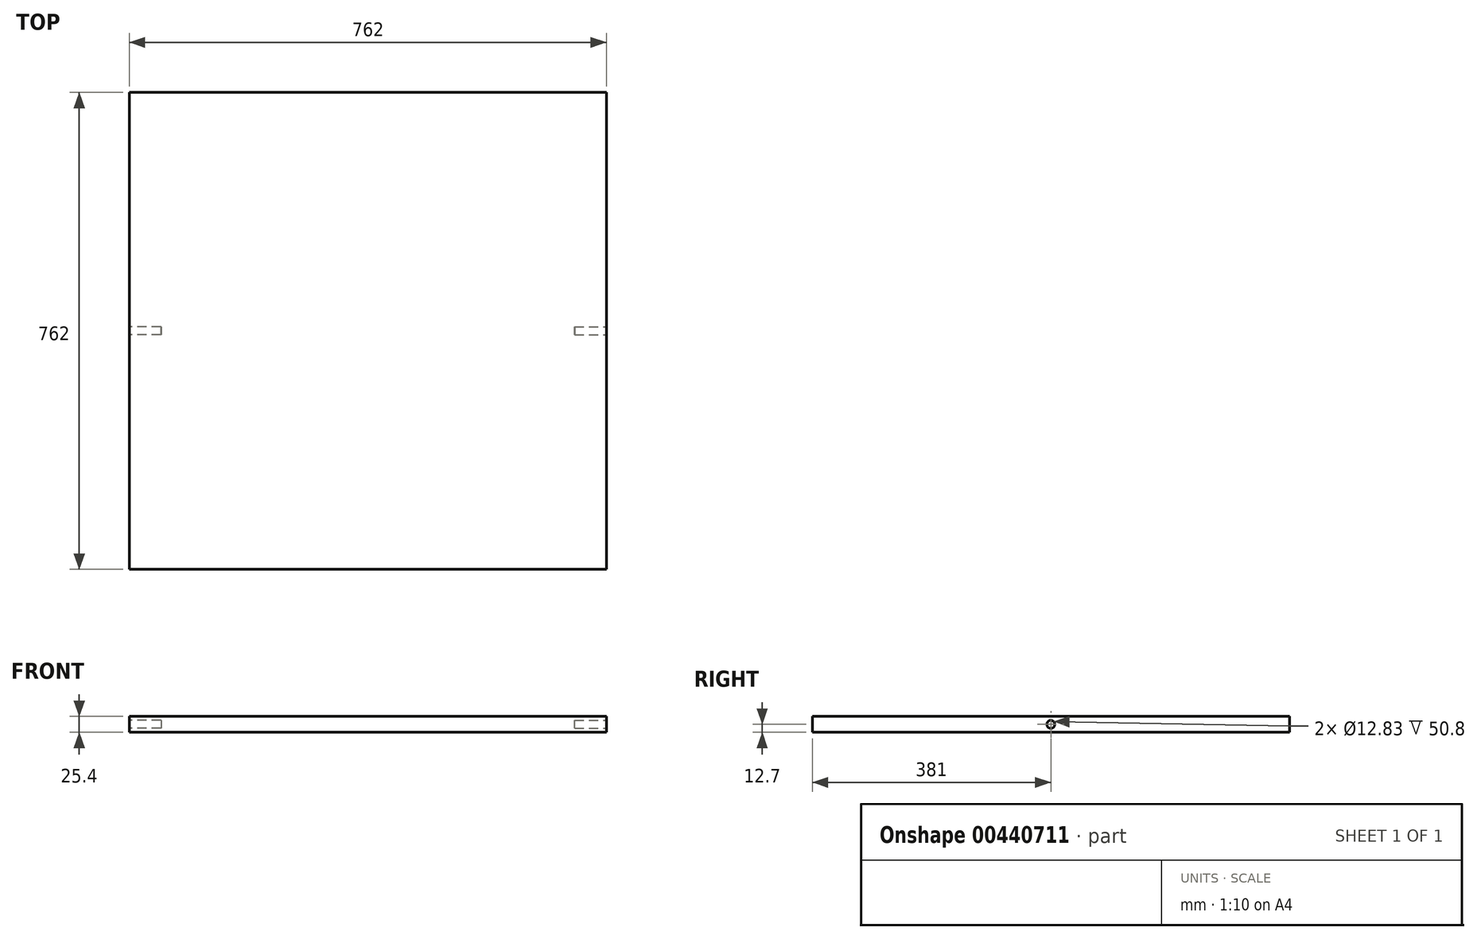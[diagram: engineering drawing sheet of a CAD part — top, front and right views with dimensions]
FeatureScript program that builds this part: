
annotation { "Feature Type Name" : "Feature", "Feature Type Description" : "" }
export const myFeature = defineFeature(function(context is Context, id is Id, definition is map)
    precondition{}
    {
        {
            var Q0;
            Q0=qCreatedBy(makeId("Top.planeOp"),FACE);
            var sketch = newSketch(context, id + "F0", { "sketchPlane" : qUnion([Q0])});
            skLineSegment(sketch, "E0.bottom", {"start": v(-381, 381) * mm, "end": v(381, 381) * mm});
            skLineSegment(sketch, "E0.top", {"start": v(-381, -381) * mm, "end": v(381, -381) * mm});
            skLineSegment(sketch, "E0.left", {"start": v(-381, 381) * mm, "end": v(-381, -381) * mm});
            skLineSegment(sketch, "E0.right", {"start": v(381, 381) * mm, "end": v(381, -381) * mm});
            skPoint(sketch, "E0.middle", {"position": v(0, 0) * mm});
            skSolve(sketch);
        }
        {
            var Q0;
            Q0 = qSketchRegion(id + "F0", true);
            extrude(context, id + "F1", {"entities" : qUnion([Q0]), "depth" : 25.4 * mm});
        }
        {
            var Q0;
            Q0=makeQuery(id+"F1.opExtrude","SWEPT_FACE",FACE,{"disambiguationData":[OSD([sQuery(id+"F0.wireOp",EDGE,"E0.right")])]});
            var sketch = newSketch(context, id + "F2", { "sketchPlane" : qUnion([Q0])});
            skCircle(sketch, "E1", {"center": v(0, 12.7) * mm, "radius": 6.41 * mm});
            skPoint(sketch, "E1.centerSnap0", {"position": v(0, 0) * mm});
            skSolve(sketch);
        }
        {
            var Q0;
            Q0 = qSketchRegion(id + "F2", true);
            extrude(context, id + "F3", {"entities" : qUnion([Q0]), "operationType" : NewBodyOperationType.REMOVE, "oppositeDirection" : true, "depth" : 50.8 * mm});
        }
        {
            var Q0;
            Q0=makeQuery(id+"F1.opExtrude","SWEPT_FACE",FACE,{"disambiguationData":[OSD([sQuery(id+"F0.wireOp",EDGE,"E0.left")])]});
            var sketch = newSketch(context, id + "F4", { "sketchPlane" : qUnion([Q0])});
            skCircle(sketch, "E2", {"center": v(0, 12.7) * mm, "radius": 6.41 * mm});
            skSolve(sketch);
        }
        {
            var Q0;
            Q0 = qSketchRegion(id + "F4", true);
            extrude(context, id + "F5", {"entities" : qUnion([Q0]), "operationType" : NewBodyOperationType.REMOVE, "oppositeDirection" : true, "depth" : 50.8 * mm});
        }
    });
